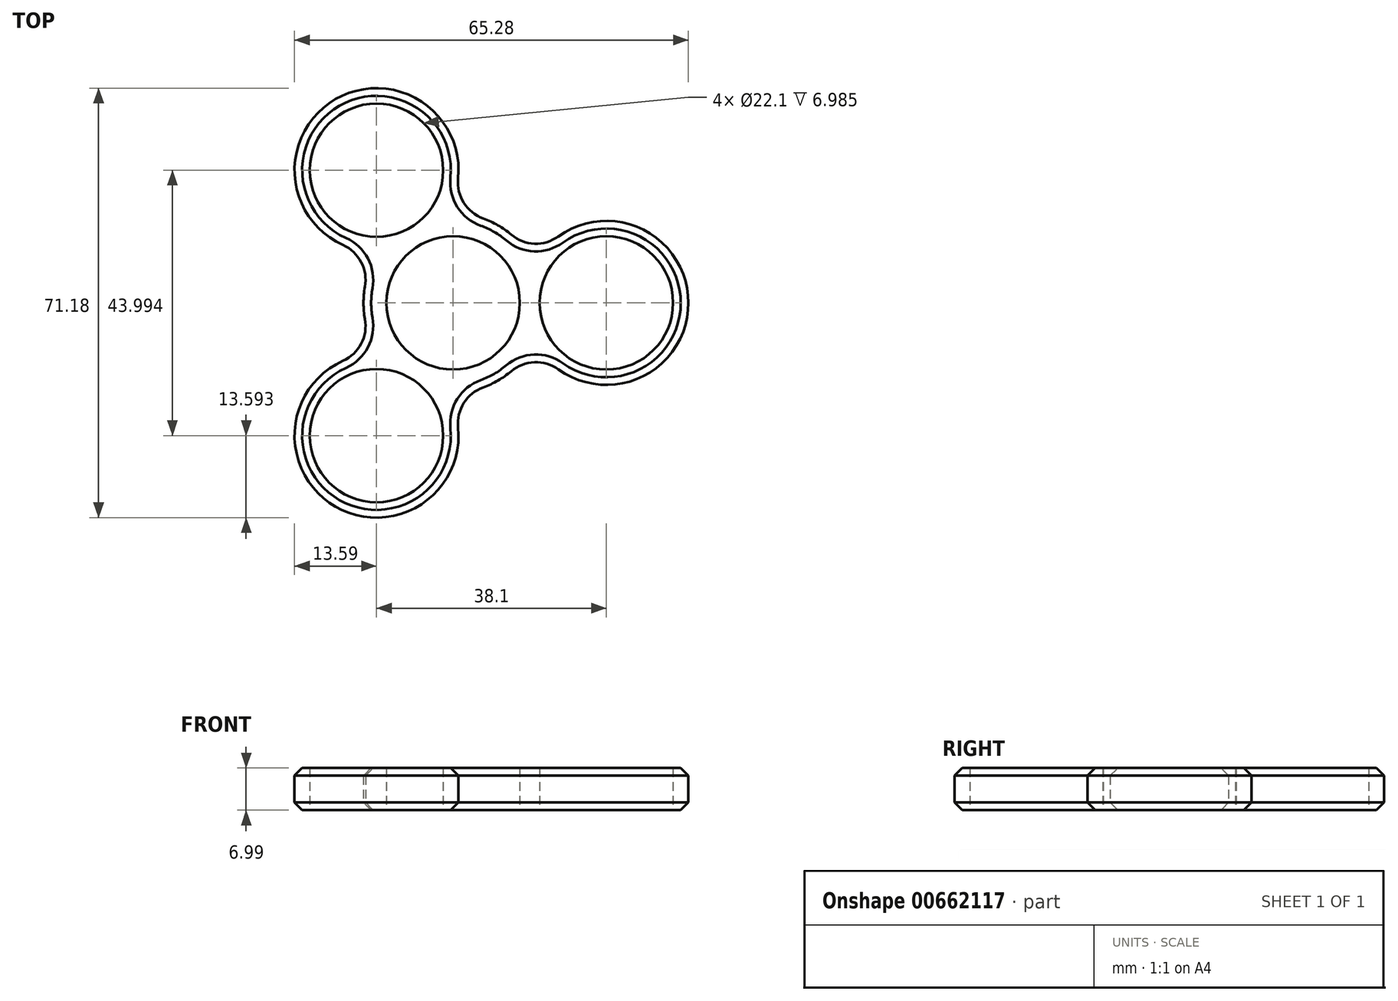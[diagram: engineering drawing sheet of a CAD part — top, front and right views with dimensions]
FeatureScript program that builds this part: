
annotation { "Feature Type Name" : "Feature", "Feature Type Description" : "" }
export const myFeature = defineFeature(function(context is Context, id is Id, definition is map)
    precondition{}
    {
        {
            var Q0;
            Q0=qCreatedBy(makeId("Top.planeOp"),FACE);
            var sketch = newSketch(context, id + "F0", { "sketchPlane" : qUnion([Q0])});
            skCircle(sketch, "E0", {"center": v(0, 0) * mm, "radius": 11.05 * mm});
            skCircle(sketch, "E1", {"center": v(25.4, 0) * mm, "radius": 11.05 * mm});
            skCircle(sketch, "E2.1.0", {"center": v(-12.7, 22) * mm, "radius": 11.05 * mm});
            skCircle(sketch, "E2.2.0", {"center": v(-12.7, -22) * mm, "radius": 11.05 * mm});
            skArc(sketch, "E3.0", {"start": v(0.82, 20.62) * mm, "mid": v(-19.5, 33.77) * mm, "end": v(-18.26, 9.6) * mm});
            skArc(sketch, "E4.0", {"start": v(17.45, -11.02) * mm, "mid": v(38.99, 0) * mm, "end": v(17.45, 11.02) * mm});
            skArc(sketch, "E5.0", {"start": v(-18.26, -9.6) * mm, "mid": v(-19.5, -33.77) * mm, "end": v(0.82, -20.62) * mm});
            skArc(sketch, "E6.0", {"start": v(-14.62, 2.67) * mm, "mid": v(-14.86, 0) * mm, "end": v(-14.62, -2.67) * mm});
            skArc(sketch, "E7.trimOffspring", {"start": v(9.62, 11.33) * mm, "mid": v(7.43, 12.87) * mm, "end": v(5, 14) * mm});
            skArc(sketch, "E8.trimOffspring", {"start": v(5, -14) * mm, "mid": v(7.43, -12.87) * mm, "end": v(9.62, -11.33) * mm});
            skPoint(sketch, "E9.visualSharp", {"position": v(13.41, -6.4) * mm});
            skArc(sketch, "E9.filletArc", {"start": v(17.45, -11.02) * mm, "mid": v(13.48, -9.82) * mm, "end": v(9.62, -11.33) * mm});
            skPoint(sketch, "E10.visualSharp", {"position": v(-1.17, -14.81) * mm});
            skArc(sketch, "E10.filletArc", {"start": v(5, -14) * mm, "mid": v(1.77, -16.58) * mm, "end": v(0.82, -20.62) * mm});
            skPoint(sketch, "E11.visualSharp", {"position": v(-12.25, -8.42) * mm});
            skArc(sketch, "E11.filletArc", {"start": v(-18.26, -9.6) * mm, "mid": v(-15.24, -6.76) * mm, "end": v(-14.62, -2.67) * mm});
            skPoint(sketch, "E12.visualSharp", {"position": v(-12.25, 8.42) * mm});
            skArc(sketch, "E12.filletArc", {"start": v(-14.62, 2.67) * mm, "mid": v(-15.24, 6.76) * mm, "end": v(-18.26, 9.6) * mm});
            skPoint(sketch, "E13.visualSharp", {"position": v(-1.17, 14.81) * mm});
            skArc(sketch, "E13.filletArc", {"start": v(0.82, 20.62) * mm, "mid": v(1.77, 16.58) * mm, "end": v(5, 14) * mm});
            skPoint(sketch, "E14.visualSharp", {"position": v(13.41, 6.4) * mm});
            skArc(sketch, "E14.filletArc", {"start": v(9.62, 11.33) * mm, "mid": v(13.48, 9.82) * mm, "end": v(17.45, 11.02) * mm});
            skSolve(sketch);
        }
        {
            var Q0;
            Q0=makeQuery(id+"F0.imprint","IMPRINT",FACE,{"disambiguationData":[TD([[makeQuery(id+"F0.imprint","IMPRINT",EDGE,{"derivedFrom":sQuery(id+"F0.wireOp",EDGE,"E0")}),-1.0]])]});
            extrude(context, id + "F1", {"entities" : qUnion([Q0]), "depth" : 7 * mm, "offsetDistance" : 25.4 * mm});
        }
        {
            var Q0;
            Q0=makeQuery(id+"F1.opExtrude","CAP_EDGE",EDGE,{"disambiguationData":[OSD([sQuery(id+"F0.wireOp",EDGE,"E5.0")])],"isStart":false});
            var Q1;
            Q1=makeQuery(id+"F1.opExtrude","CAP_EDGE",EDGE,{"disambiguationData":[OSD([sQuery(id+"F0.wireOp",EDGE,"E10.filletArc")])],"isStart":true});
            chamfer(context, id + "F2", {"entities" : qUnion([Q0, Q1]), "width" : 1.27 * mm, "tangentPropagation" : true});
        }
    });
